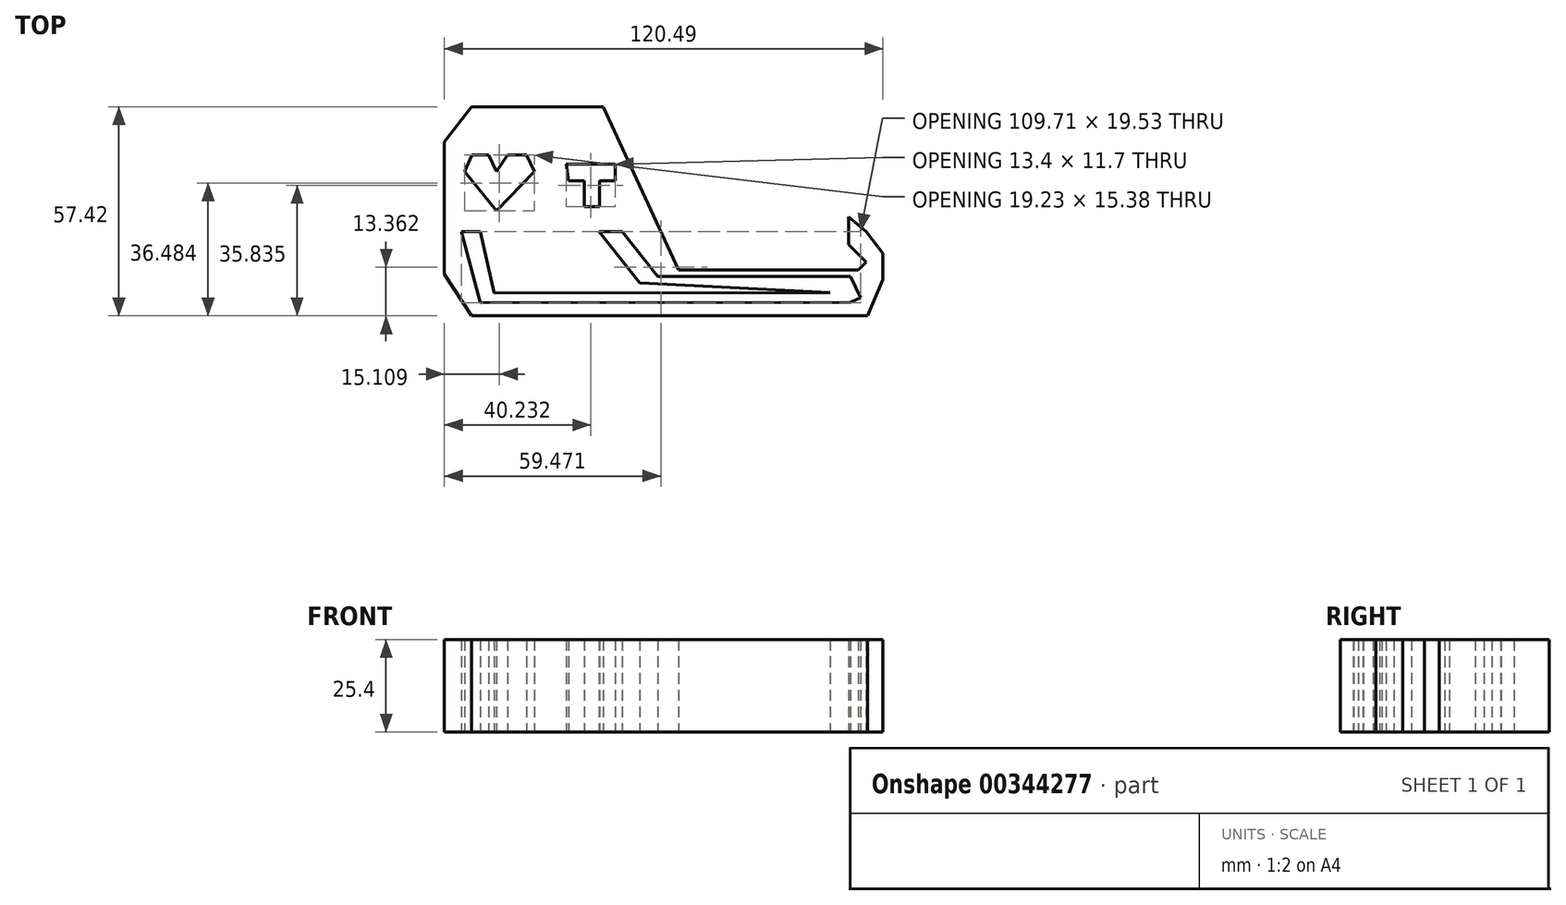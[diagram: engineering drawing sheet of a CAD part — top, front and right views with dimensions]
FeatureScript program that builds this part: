
annotation { "Feature Type Name" : "Feature", "Feature Type Description" : "" }
export const myFeature = defineFeature(function(context is Context, id is Id, definition is map)
    precondition{}
    {
        {
            var Q0;
            Q0=qCreatedBy(makeId("Top.planeOp"),FACE);
            var sketch = newSketch(context, id + "F0", { "sketchPlane" : qUnion([Q0])});
            skLineSegment(sketch, "E0", {"start": v(-60.35, 34.3) * mm, "end": v(-67.76, 24.66) * mm});
            skLineSegment(sketch, "E1", {"start": v(-67.76, 24.66) * mm, "end": v(-67.76, -11.73) * mm});
            skLineSegment(sketch, "E2", {"start": v(-67.76, -11.73) * mm, "end": v(-60.35, -23.13) * mm});
            skLineSegment(sketch, "E3", {"start": v(-60.35, -23.13) * mm, "end": v(48.55, -23.13) * mm});
            skLineSegment(sketch, "E4", {"start": v(52.73, -13.26) * mm, "end": v(52.73, -5.94) * mm});
            skLineSegment(sketch, "E5", {"start": v(52.73, -5.94) * mm, "end": v(48.16, 0) * mm});
            skLineSegment(sketch, "E6", {"start": v(48.16, 0) * mm, "end": v(43.28, 4.11) * mm});
            skLineSegment(sketch, "E7", {"start": v(43.28, 4.11) * mm, "end": v(43.28, -3.5) * mm});
            skLineSegment(sketch, "E8", {"start": v(43.28, -3.5) * mm, "end": v(48.16, -8.38) * mm});
            skLineSegment(sketch, "E9", {"start": v(48.16, -8.38) * mm, "end": v(46, -10.54) * mm});
            skLineSegment(sketch, "E10", {"start": v(46, -10.54) * mm, "end": v(-3.43, -10.54) * mm});
            skLineSegment(sketch, "E11", {"start": v(-60.35, 34.3) * mm, "end": v(-24.08, 34.3) * mm});
            skLineSegment(sketch, "E12", {"start": v(-24.08, 34.3) * mm, "end": v(-3.43, -10.54) * mm});
            skLineSegment(sketch, "E13", {"start": v(-63.14, 0) * mm, "end": v(-57.91, 0) * mm});
            skLineSegment(sketch, "E14", {"start": v(-18.95, 0) * mm, "end": v(-9.14, -12.34) * mm});
            skLineSegment(sketch, "E15", {"start": v(-57.91, -19.53) * mm, "end": v(-63.14, 0) * mm});
            skLineSegment(sketch, "E16", {"start": v(-9.14, -12.34) * mm, "end": v(43.87, -12.34) * mm});
            skLineSegment(sketch, "E17", {"start": v(52.73, -13.26) * mm, "end": v(48.55, -23.13) * mm});
            skPoint(sketch, "E18.endSnap0", {"position": v(50.64, -18.2) * mm});
            skLineSegment(sketch, "E19", {"start": v(46.57, -18.2) * mm, "end": v(43.87, -19.44) * mm});
            skLineSegment(sketch, "E20", {"start": v(43.87, -19.44) * mm, "end": v(-57.91, -19.53) * mm});
            skLineSegment(sketch, "E21", {"start": v(-57.91, 0) * mm, "end": v(-54.05, -16.83) * mm});
            skLineSegment(sketch, "E22", {"start": v(-54.05, -16.83) * mm, "end": v(38.24, -16.74) * mm});
            skLineSegment(sketch, "E23", {"start": v(43.87, -12.34) * mm, "end": v(46.57, -18.2) * mm});
            skLineSegment(sketch, "E24", {"start": v(-18.95, 0) * mm, "end": v(-25.28, 0) * mm});
            skLineSegment(sketch, "E25", {"start": v(-25.28, 0) * mm, "end": v(-14.14, -14.03) * mm});
            skLineSegment(sketch, "E26", {"start": v(-14.14, -14.03) * mm, "end": v(38.24, -16.74) * mm});
            skLineSegment(sketch, "E27", {"start": v(-34.23, 18.54) * mm, "end": v(-20.83, 18.56) * mm});
            skLineSegment(sketch, "E28", {"start": v(-20.83, 18.56) * mm, "end": v(-20.83, 13.98) * mm});
            skLineSegment(sketch, "E29", {"start": v(-20.83, 13.98) * mm, "end": v(-25.1, 13.98) * mm});
            skLineSegment(sketch, "E30", {"start": v(-25.1, 13.98) * mm, "end": v(-25.1, 6.86) * mm});
            skLineSegment(sketch, "E31", {"start": v(-25.1, 6.86) * mm, "end": v(-29.38, 6.85) * mm});
            skLineSegment(sketch, "E32", {"start": v(-29.38, 6.85) * mm, "end": v(-29.4, 13.98) * mm});
            skLineSegment(sketch, "E33", {"start": v(-29.4, 13.98) * mm, "end": v(-33.66, 13.98) * mm});
            skLineSegment(sketch, "E34", {"start": v(-33.66, 13.98) * mm, "end": v(-34.23, 18.54) * mm});
            skLineSegment(sketch, "E35", {"start": v(-60.23, 21.04) * mm, "end": v(-55.6, 21.04) * mm});
            skLineSegment(sketch, "E36", {"start": v(-55.6, 21.04) * mm, "end": v(-53.48, 16.46) * mm});
            skLineSegment(sketch, "E37", {"start": v(-53.48, 16.46) * mm, "end": v(-50.37, 21.05) * mm});
            skLineSegment(sketch, "E38", {"start": v(-50.37, 21.05) * mm, "end": v(-45.15, 21.05) * mm});
            skLineSegment(sketch, "E39", {"start": v(-45.15, 21.05) * mm, "end": v(-43.04, 16.46) * mm});
            skLineSegment(sketch, "E40", {"start": v(-43.04, 16.46) * mm, "end": v(-53.48, 5.66) * mm});
            skLineSegment(sketch, "E41", {"start": v(-53.48, 5.66) * mm, "end": v(-62.26, 16.46) * mm});
            skLineSegment(sketch, "E42", {"start": v(-62.26, 16.46) * mm, "end": v(-60.23, 21.04) * mm});
            skSolve(sketch);
        }
        {
            var Q0;
            Q0 = qSketchRegion(id + "F0", true);
            extrude(context, id + "F1", {"entities" : qUnion([Q0]), "depth" : 25.4 * mm});
        }
    });
